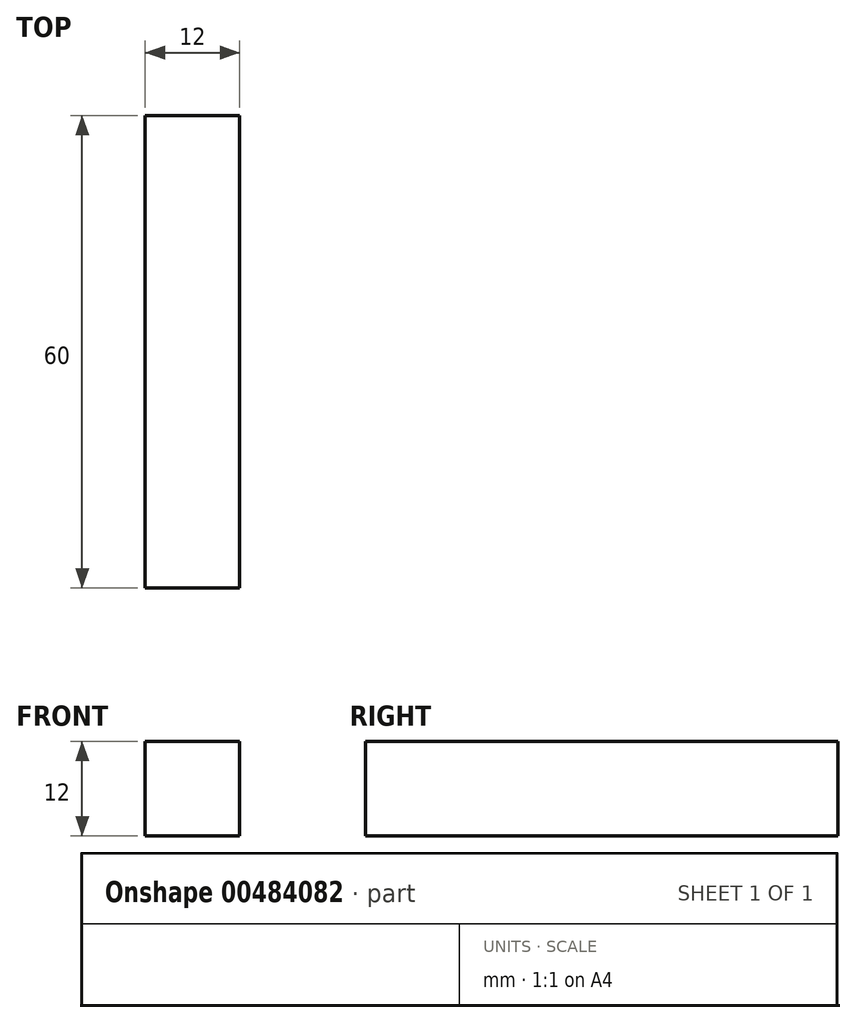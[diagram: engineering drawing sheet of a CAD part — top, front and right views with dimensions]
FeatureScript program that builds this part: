
annotation { "Feature Type Name" : "Feature", "Feature Type Description" : "" }
export const myFeature = defineFeature(function(context is Context, id is Id, definition is map)
    precondition{}
    {
        {
            var Q0;
            Q0=qCreatedBy(makeId("Front.planeOp"),FACE);
            var sketch = newSketch(context, id + "F0", { "sketchPlane" : qUnion([Q0])});
            skLineSegment(sketch, "E0.bottom", {"start": v(-38.33, 0) * mm, "end": v(-26.33, 0) * mm});
            skLineSegment(sketch, "E0.top", {"start": v(-38.33, -12) * mm, "end": v(-26.33, -12) * mm});
            skLineSegment(sketch, "E0.left", {"start": v(-38.33, 0) * mm, "end": v(-38.33, -12) * mm});
            skLineSegment(sketch, "E0.right", {"start": v(-26.33, 0) * mm, "end": v(-26.33, -12) * mm});
            skSolve(sketch);
        }
        {
            var Q0;
            Q0 = qSketchRegion(id + "F0", true);
            extrude(context, id + "F1", {"entities" : qUnion([Q0]), "depth" : 60 * mm, "offsetDistance" : 25 * mm});
        }
    });
